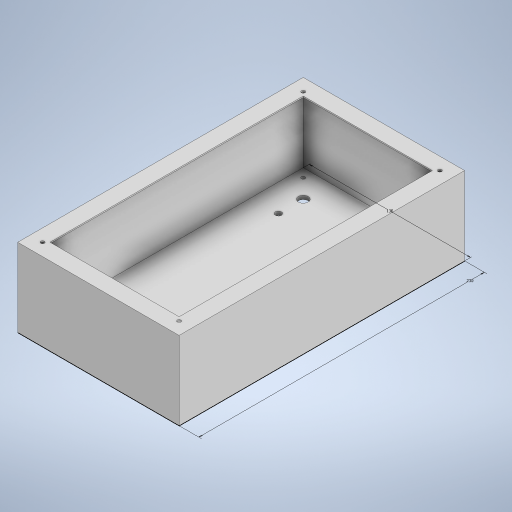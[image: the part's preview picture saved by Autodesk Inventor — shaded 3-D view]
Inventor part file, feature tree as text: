
AUTODESK INVENTOR PART (.ipt)
format: ipt  version: 2024 (Build 280153000, 153)  size: 354,304 bytes
history: native  units: mm
features: sketch x9, extrude x9, other x1
ambient origin geometry x8: Origin, YZ Plane, XZ Plane, XY Plane, X Axis, Y Axis, Z Axis, Center Point
bodies: Body1 (feature_tree)
feature tree (19):
  other  "Sólido1"
  sketch  "Boceto1"  dims[d0=130.0mm d1=230.0mm]
  extrude  "Extrusión1"  Depth=230.0mm
  extrude  "Extrusión2"  Depth=3.0mm
  extrude  "Extrusión3"  Depth=1.0mm
  extrude  "Extrusión4"  Depth=10.0mm
  extrude  "Extrusión5"  Depth=10.0mm TaperAngle=0.0deg
  extrude  "Extrusión6"  TaperAngle=0.0deg  [1 undecoded]
  extrude  "Extrusión7"  Depth=211.5mm TaperAngle=0.0deg
  extrude  "Extrusión8"  Depth=3.0mm
  extrude  "Extrusión9"  Depth=3.0mm
  sketch  "Boceto2"  dims[d2=3.0mm d3=0.0mm d4=3.0mm]
  sketch  "Boceto3"  dims[d5=60.0mm d6=0.0mm d7=1.0mm]
  sketch  "Boceto4"  dims[d8=10.0mm d9=0.0mm d10=10.0mm]
  sketch  "Boceto5"  dims[d11=10.0mm d12=115.25mm d13=0.0mm]
  sketch  "Boceto6"  dims[d14=10.0mm d15=0.0mm]
  sketch  "Boceto7"  dims[d16=0.0mm d17=211.5mm d18=0.0mm]
  sketch  "Boceto8"  dims[d19=3.0mm d20=3.0mm]
  sketch  "Boceto9"  dims[d21=3.0mm d22=3.0mm d23=10.0mm d24=10.0mm d25=10.0mm d26=10.0mm d27=10.0mm d28=10.0mm d29=10.0mm d30=10.0mm d31=211.5mm d32=0.0mm d33=8.0mm d34=8.0mm d35=8.0mm d36=8.0mm d37=25.0mm d38=25.0mm d39=25.0mm d40=25.0mm d41=25.0mm d42=25.0mm d43=25.0mm d44=25.0mm d45=10.0mm d46=0.0mm d47=70.0mm d48=10.0mm d49=35.0mm d50=30.0mm d51=30.0mm d52=5.0mm d53=5.0mm d54=5.0mm d55=5.0mm d56=5.0mm d57=5.0mm d58=10.0mm d59=0.0mm d60=90.0mm d61=130.0mm d62=20.0mm d63=20.0mm d64=60.0mm d65=5.0mm d66=5.0mm d67=5.0mm d68=5.0mm d69=5.0mm d70=5.0mm d71=5.0mm d72=5.0mm d73=5.0mm d74=5.0mm d75=5.0mm d76=5.0mm d77=10.0mm d78=0.0mm]
note: 1 required parameter value undecoded (feature->parameter linkage not recoverable at this tier; creation-order binding heuristic only, values carry confidence <= 0.55)
